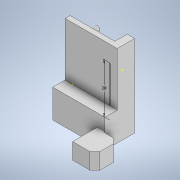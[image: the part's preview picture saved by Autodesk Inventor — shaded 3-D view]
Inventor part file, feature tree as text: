
AUTODESK INVENTOR PART (.ipt)
format: ipt  version: 2021 (Build 250183000, 183)  size: 343,552 bytes
history: native  units: mm
features: sketch x19, extrude x18, other x1, chamfer x1, plane x1, mirror x1
ambient origin geometry x8: Origin, YZ Plane, XZ Plane, XY Plane, X Axis, Y Axis, Z Axis, Center Point
bodies: Body1 (feature_tree)
feature tree (41):
  other  "Sólido1"
  extrude  "Extrusión1"  Depth=9.5mm
  extrude  "Extrusión2"  Depth=14.0mm
  extrude  "Extrusión3"  Depth=2.0mm
  chamfer  "Chaflán1"  Distance=2.0mm
  extrude  "Extrusión4"  Depth=5.0mm
  extrude  "Extrusión5"  Depth=6.0mm
  extrude  "Extrusión6"  Depth=5.0mm
  extrude  "Extrusión7"  Depth=1.25mm
  extrude  "Extrusión8"  Depth=5.0mm
  extrude  "Extrusión9"  Depth=2.0mm TaperAngle=45.0deg
  sketch  "Boceto11"  dims[d19=1.0mm d20=0.0mm d21=2.0mm d22=2.0mm d23=45.0deg]
  plane  "Plano de trabajo1"
  mirror  "Simetría1"
  extrude  "Extrusión10"  Depth=5.0mm
  extrude  "Extrusión11"  Depth=7.5mm
  extrude  "Extrusión12"  Depth=5.0mm
  extrude  "Extrusión13"  Depth=6.0mm
  extrude  "Extrusión14"  Depth=5.0mm
  extrude  "Extrusión15"  Depth=2.5mm
  extrude  "Extrusión16"  Depth=3.0mm TaperAngle=0.0deg
  extrude  "Extrusión17"  Depth=8.0mm TaperAngle=0.0deg
  extrude  "Extrusión18"  Depth=2.0mm
  sketch  "Boceto21"  dims[d46=2.0mm d47=6.0mm d51=6.0mm d52=0.0mm d53=0.5mm d54=0.0mm d55=5.0mm d56=0.0mm d58=20.0mm d59=10.0mm d60=4.0mm d61=0.0mm d62=9.0mm d63=0.0mm d64=6.5mm d65=0.0mm d66=10.0mm d67=2.0mm d68=2.0mm d69=10.0mm d70=2.0mm d71=0.0mm d72=10.0mm d73=10.0mm d74=2.0mm d75=2.0mm d76=6.0mm d77=0.0mm d78=6.0mm d79=0.0mm d80=5.0mm d81=0.0mm d82=10.0mm d83=2.0mm d84=10.0mm d85=2.0mm d86=5.0mm d87=5.0mm d88=0.0mm d89=6.5mm d90=0.0mm]
  sketch  "Boceto1"  dims[d0=4.0mm d1=9.5mm]
  sketch  "Boceto3"  dims[d2=4.0mm d3=0.0mm d4=14.0mm]
  sketch  "Boceto4"  dims[d5=3.0mm d6=20.0mm d7=2.0mm d8=0.0mm]
  sketch  "Boceto5"  dims[d9=5.0mm d10=2.5mm]
  sketch  "Boceto7"  dims[d11=6.0mm d12=6.0mm]
  sketch  "Boceto8"  dims[d13=2.5mm d14=5.0mm]
  sketch  "Boceto9"  dims[d15=2.5mm d16=1.25mm]
  sketch  "Boceto10"  dims[d17=5.0mm d18=2.5mm]
  sketch  "Boceto12"  dims[d25=7.5mm d26=5.0mm]
  sketch  "Boceto13"  dims[d27=20.0mm d28=7.5mm]
  sketch  "Boceto14"  dims[d29=5.0mm d30=2.5mm]
  sketch  "Boceto15"  dims[d31=6.0mm d32=6.0mm]
  sketch  "Boceto16"  dims[d33=5.0mm d34=2.5mm]
  sketch  "Boceto17"  dims[d35=1.25mm d36=2.5mm]
  sketch  "Boceto18"  dims[d37=3.0mm d38=0.0mm d39=2.5mm d40=0.0mm]
  sketch  "Boceto19"  dims[d41=2.0mm d42=8.0mm d43=0.0mm]
  sketch  "Boceto20"  dims[d44=2.0mm d45=4.0mm]
